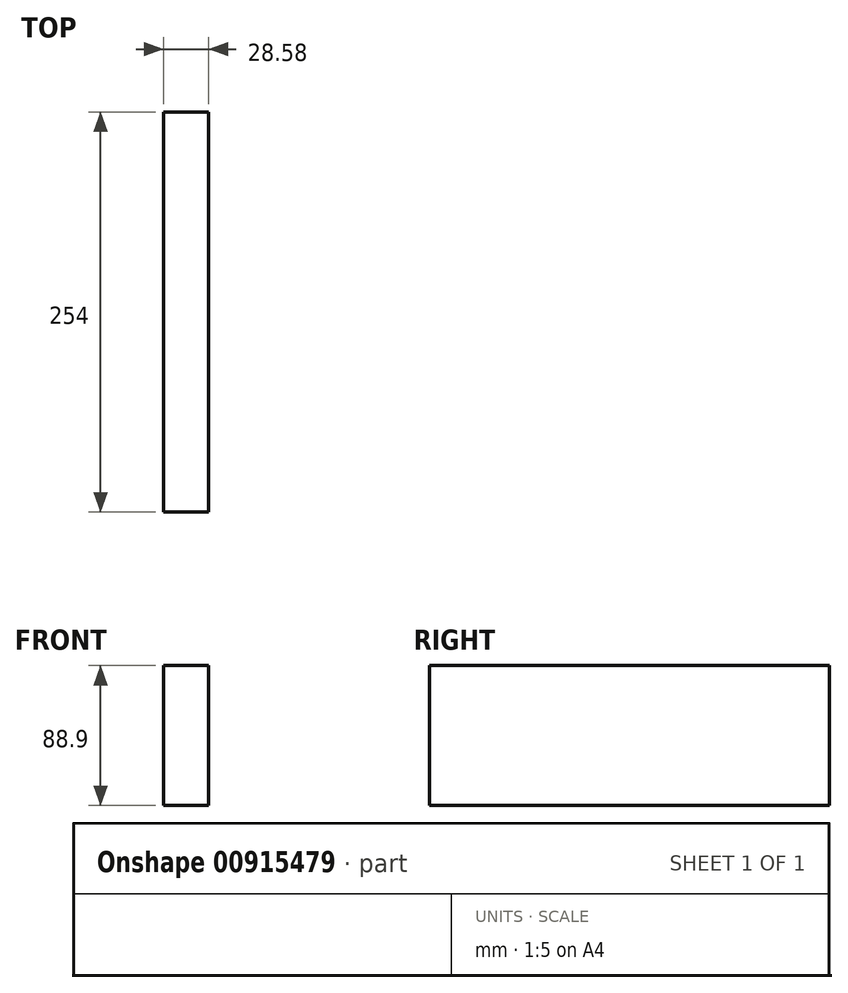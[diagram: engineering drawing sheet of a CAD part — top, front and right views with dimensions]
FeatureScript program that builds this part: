
annotation { "Feature Type Name" : "Feature", "Feature Type Description" : "" }
export const myFeature = defineFeature(function(context is Context, id is Id, definition is map)
    precondition{}
    {
        {
            var Q0;
            Q0=qCreatedBy(makeId("Front.planeOp"),FACE);
            var sketch = newSketch(context, id + "F0", { "sketchPlane" : qUnion([Q0])});
            skLineSegment(sketch, "E0.bottom", {"start": v(14.29, 44.45) * mm, "end": v(-14.29, 44.45) * mm});
            skLineSegment(sketch, "E0.top", {"start": v(14.29, -44.45) * mm, "end": v(-14.29, -44.45) * mm});
            skLineSegment(sketch, "E0.left", {"start": v(14.29, 44.45) * mm, "end": v(14.29, -44.45) * mm});
            skLineSegment(sketch, "E0.right", {"start": v(-14.29, 44.45) * mm, "end": v(-14.29, -44.45) * mm});
            skPoint(sketch, "E0.middle", {"position": v(0, 0) * mm});
            skSolve(sketch);
        }
        {
            var Q0;
            Q0=makeQuery(id+"F0.imprint","IMPRINT",FACE,{"disambiguationData":[TD([[makeQuery(id+"F0.imprint","IMPRINT",EDGE,{"derivedFrom":sQuery(id+"F0.wireOp",EDGE,"E0.bottom")}),1.0]])]});
            extrude(context, id + "F1", {"entities" : qUnion([Q0]), "depth" : 254 * mm, "offsetDistance" : 25.4 * mm});
        }
    });
